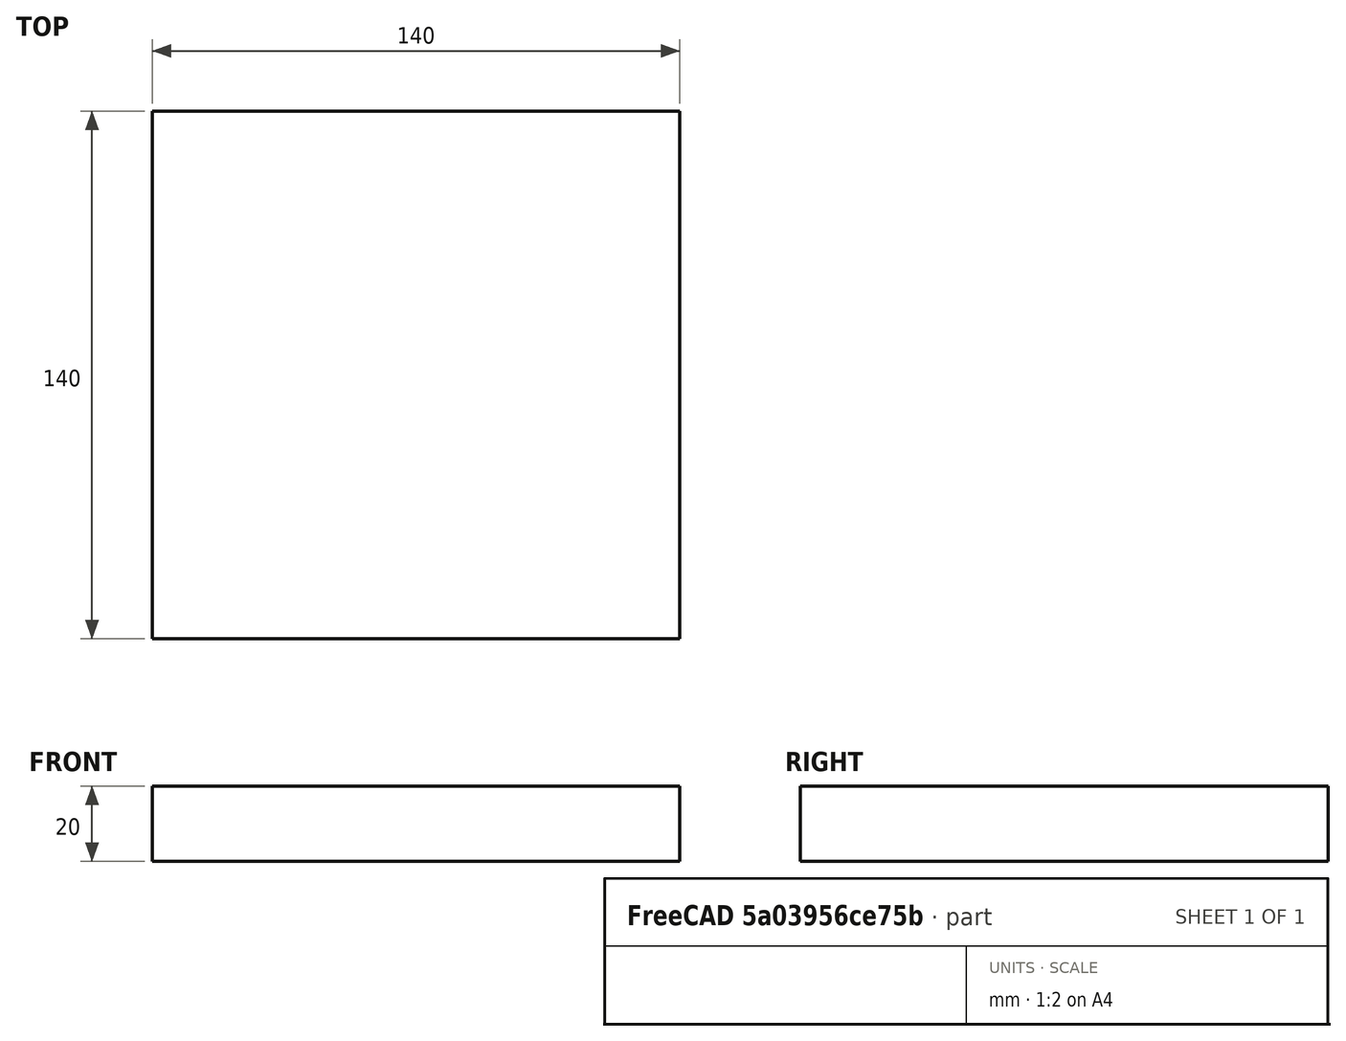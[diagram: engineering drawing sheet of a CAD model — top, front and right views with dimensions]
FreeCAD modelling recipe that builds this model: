
FCSTD DOCUMENT  (FreeCAD 0.19R24291 (Git))
Label: base_robot_def
License: All rights reserved
LicenseURL: http://en.wikipedia.org/wiki/All_rights_reserved
objects: TechDraw::DrawProjGroupItem×3, Sketcher::SketchObject×1, PartDesign::Pad×1, PartDesign::Body×1, TechDraw::DrawSVGTemplate×1, TechDraw::DrawProjGroup×1, TechDraw::DrawPage×1
note: 4 computed .brp shape members not serialized (recipe doc carries the construction recipe); baked Part::Feature solids carry a one-line shape summary decoded from their .brp

FEATURE [Sketcher::SketchObject] Sketch
  FullyConstrained = false
  MapMode = 5
  Support = -> [XY_Plane]
  sketch-geometry (4):
    g0: LineSegment StartX=-70.5237 StartY=57.5569 StartZ=0 EndX=69.4763 EndY=57.5569 EndZ=0
    g1: LineSegment StartX=69.4763 StartY=57.5569 StartZ=0 EndX=69.4763 EndY=-82.4431 EndZ=0
    g2: LineSegment StartX=69.4763 StartY=-82.4431 StartZ=0 EndX=-70.5237 EndY=-82.4431 EndZ=0
    g3: LineSegment StartX=-70.5237 StartY=-82.4431 StartZ=0 EndX=-70.5237 EndY=57.5569 EndZ=0
  constraints (10):
    c: Coincident(g0,g1)
    c: Coincident(g1,g2)
    c: Coincident(g2,g3)
    c: Coincident(g3,g0)
    c: Horizontal(g0)
    c: Horizontal(g2)
    c: Vertical(g1)
    c: Vertical(g3)
    c: DistanceX(g0,g0) = 140
    c: DistanceY(g1,g1) = 140
FEATURE [PartDesign::Pad] Pad
  Direction = (1,1,1)
  Length = 20
  Length2 = 100
  Profile = -> Sketch
  Type = 0
FEATURE [PartDesign::Body] Body  label="base"
  Group = -> [Sketch,Pad]
  Origin = -> Origin
  Tip = -> Pad
FEATURE [TechDraw::DrawSVGTemplate] Template
  EditableTexts = Designed_by_Name=Los legendarios; Drawing_number=Drawing number; FC-Date=Date; FC-SC=1:4; FC-SH=Sheet; FC-Title=Base robot; Subtitle=Subtitle; Weight=Weight
  Height = 210
  Orientation = 1
  Width = 297
FEATURE [TechDraw::DrawProjGroupItem] ProjItem  label="Front"
  CoarseView = false
  Direction = (0,0,1)
  Focus = 100
  HardHidden = false
  IsoCount = 0
  IsoHidden = false
  IsoVisible = false
  LockPosition = true
  Perspective = false
  Rotation = 0
  RotationVector = (1,0,0)
  Scale = 0.333333
  ScaleType = 2
  SeamHidden = false
  SeamVisible = true
  SmoothHidden = false
  SmoothVisible = true
  Source = -> [Body]
  Type = 0
  X = 0
  XDirection = (1,0,0)
  Y = 0
FEATURE [TechDraw::DrawProjGroupItem] ProjItem001  label="Left"
  CoarseView = false
  Direction = (-1,0,1e-16)
  Focus = 100
  HardHidden = false
  IsoCount = 0
  IsoHidden = false
  IsoVisible = false
  LockPosition = false
  Perspective = false
  Rotation = 0
  RotationVector = (1,0,0)
  Scale = 0.333333
  ScaleType = 2
  SeamHidden = false
  SeamVisible = true
  SmoothHidden = false
  SmoothVisible = true
  Source = -> [Body]
  Type = 1
  X = 41.6666
  XDirection = (1e-16,0,1)
  Y = 0
FEATURE [TechDraw::DrawProjGroupItem] ProjItem002  label="Top"
  CoarseView = false
  Direction = (0,1,0)
  Focus = 100
  HardHidden = false
  IsoCount = 0
  IsoHidden = false
  IsoVisible = false
  LockPosition = false
  Perspective = false
  Rotation = 0
  RotationVector = (1,0,0)
  Scale = 0.333333
  ScaleType = 2
  SeamHidden = false
  SeamVisible = true
  SmoothHidden = false
  SmoothVisible = true
  Source = -> [Body]
  Type = 4
  X = 0
  XDirection = (1,0,0)
  Y = -81.6666
FEATURE [TechDraw::DrawProjGroup] ProjGroup
  Anchor = -> ProjItem
  AutoDistribute = true
  LockPosition = false
  ProjectionType = 0
  Rotation = 0
  Scale = 0.333333
  ScaleType = 2
  Source = -> [Body]
  Views = -> [ProjItem,ProjItem001,ProjItem002]
  X = 111.082
  Y = 124.956
  spacingX = 15
  spacingY = 15
FEATURE [TechDraw::DrawPage] Page
  KeepUpdated = true
  NextBalloonIndex = 1
  ProjectionType = 0
  Template = -> Template
  Views = -> [ProjGroup]
